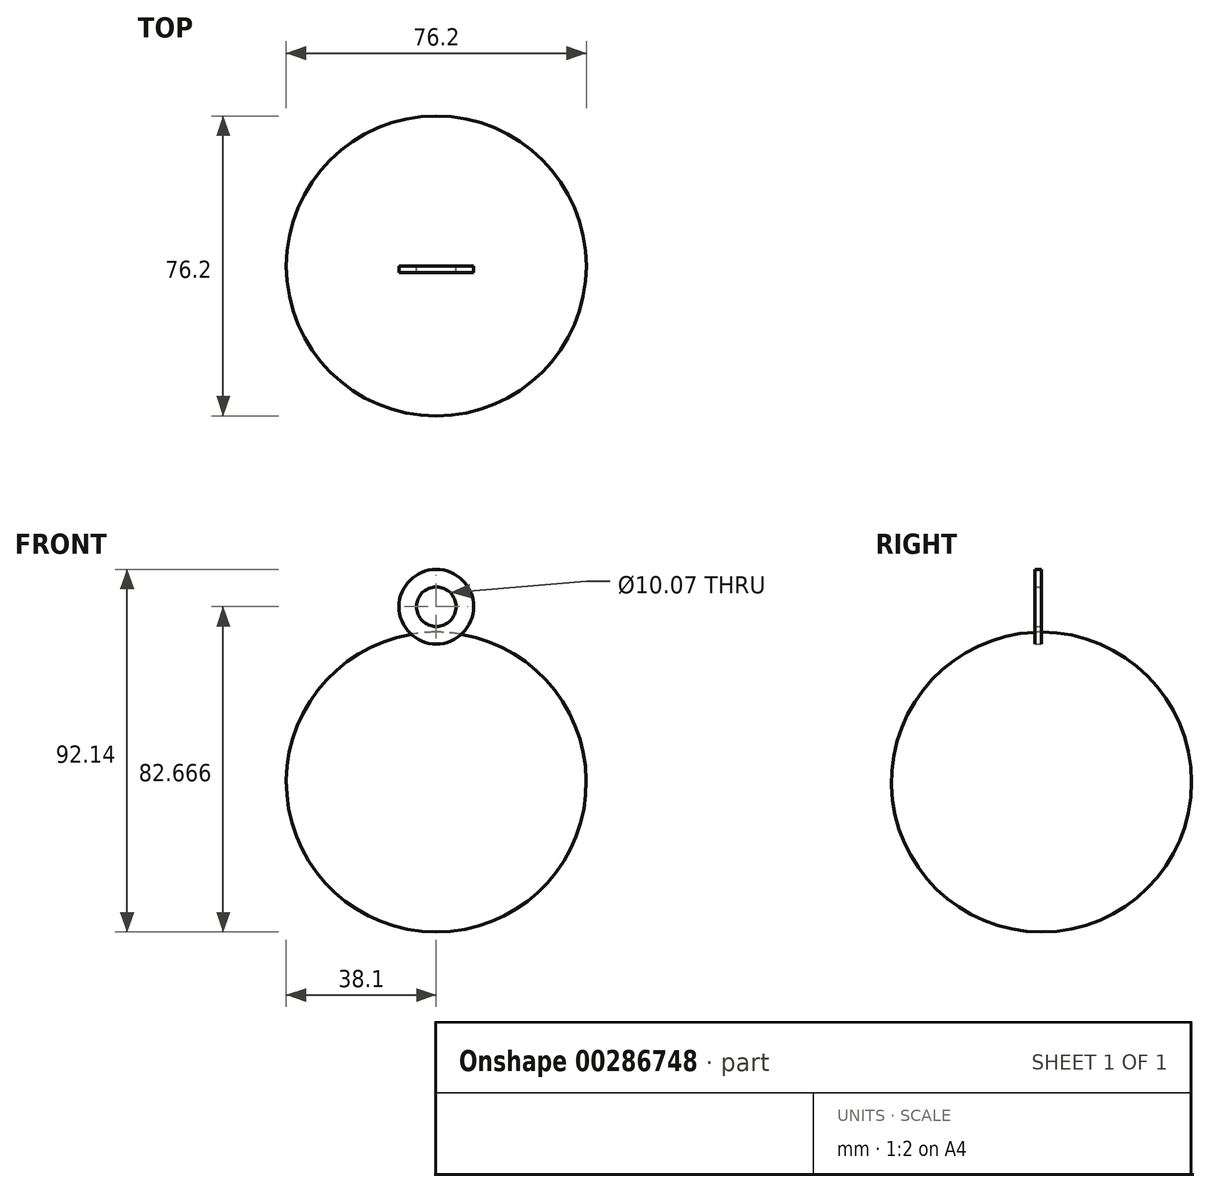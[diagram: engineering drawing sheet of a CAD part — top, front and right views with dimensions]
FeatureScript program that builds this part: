
annotation { "Feature Type Name" : "Feature", "Feature Type Description" : "" }
export const myFeature = defineFeature(function(context is Context, id is Id, definition is map)
    precondition{}
    {
        {
            var Q0;
            Q0=qCreatedBy(makeId("Front.planeOp"),FACE);
            var sketch = newSketch(context, id + "F0", { "sketchPlane" : qUnion([Q0])});
            skArc(sketch, "E0", {"start": v(0, -38.1) * mm, "mid": v(38.1, 0) * mm, "end": v(0, 38.1) * mm});
            skLineSegment(sketch, "E1", {"start": v(0, 53.17) * mm, "end": v(0, -67.24) * mm});
            skSolve(sketch);
        }
        {
            var Q0;
            Q0 = qSketchRegion(id + "F0", true);
            var Q1;
            Q1=sQuery(id+"F0.wireOp",EDGE,"E1");
            revolve(context, id + "F1", {"entities" : qUnion([Q0]), "axis" : qUnion([Q1]), "revolveType" : RevolveType.FULL});
        }
        {
            var Q0;
            Q0=qCreatedBy(makeId("Front.planeOp"),FACE);
            var sketch = newSketch(context, id + "F2", { "sketchPlane" : qUnion([Q0])});
            skCircle(sketch, "E2", {"center": v(0, 44.57) * mm, "radius": 9.48 * mm});
            skCircle(sketch, "E3", {"center": v(0, 44.57) * mm, "radius": 5.03 * mm});
            skSolve(sketch);
        }
        {
            var Q0;
            Q0=makeQuery(id+"F2.imprint","IMPRINT",FACE,{"disambiguationData":[TD([[makeQuery(id+"F2.imprint","IMPRINT",EDGE,{"derivedFrom":sQuery(id+"F2.wireOp",EDGE,"E2")}),1.0]])]});
            extrude(context, id + "F3", {"entities" : qUnion([Q0]), "depth" : 1.65 * mm});
        }
    });
